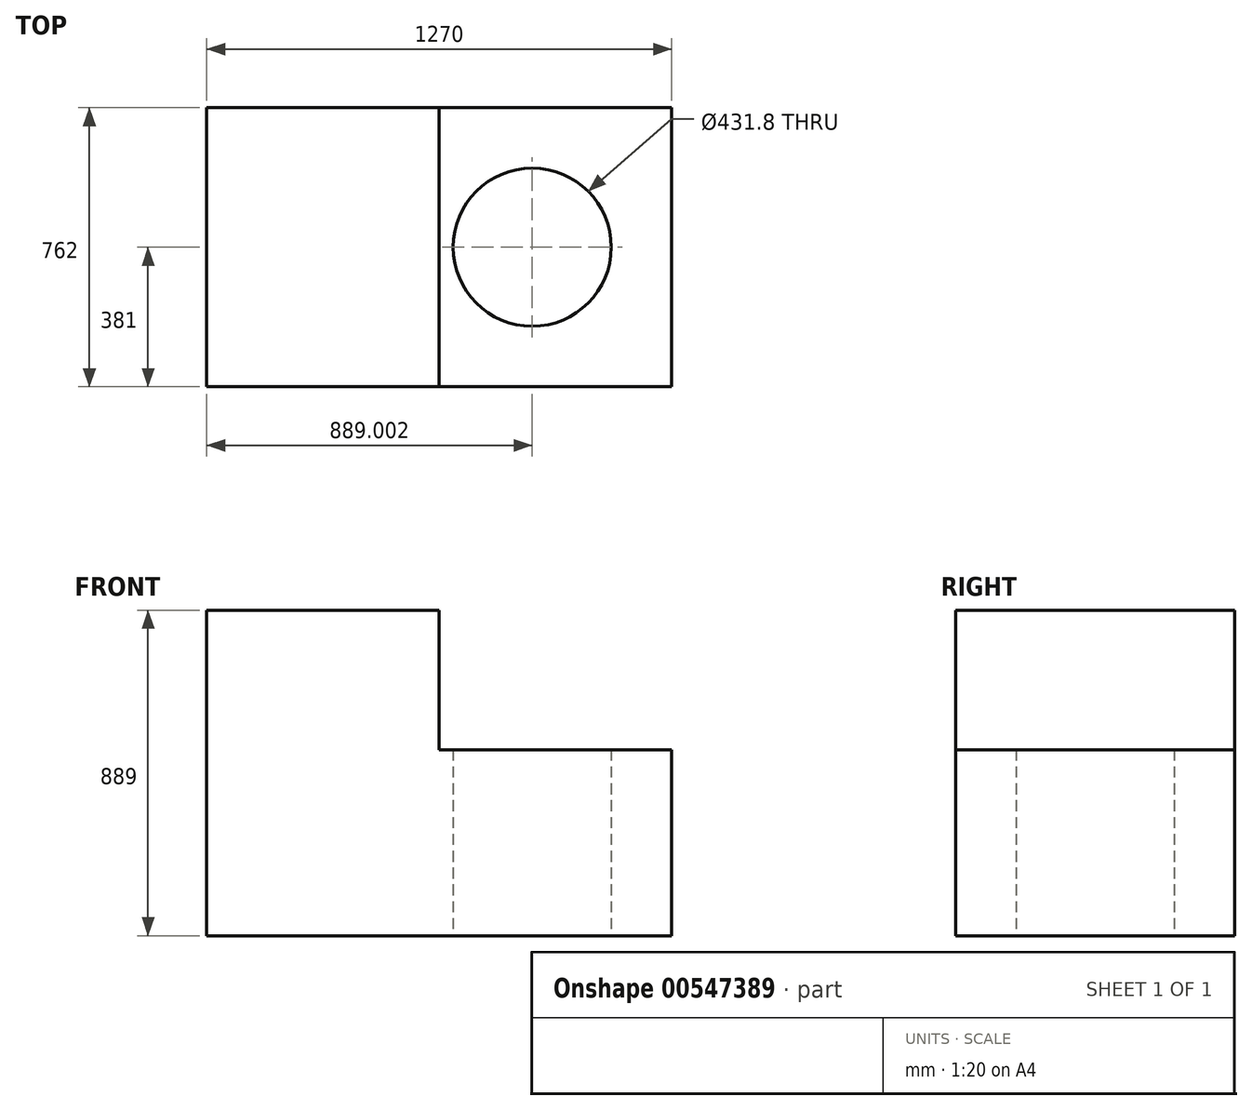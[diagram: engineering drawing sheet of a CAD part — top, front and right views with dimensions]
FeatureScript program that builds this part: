
annotation { "Feature Type Name" : "Feature", "Feature Type Description" : "" }
export const myFeature = defineFeature(function(context is Context, id is Id, definition is map)
    precondition{}
    {
        {
            var Q0;
            Q0=qCreatedBy(makeId("Front.planeOp"),FACE);
            var sketch = newSketch(context, id + "F0", { "sketchPlane" : qUnion([Q0])});
            skLineSegment(sketch, "E0", {"start": v(-633.14, -431.6) * mm, "end": v(636.86, -431.6) * mm});
            skLineSegment(sketch, "E1", {"start": v(-633.14, -431.6) * mm, "end": v(-633.14, 457.4) * mm});
            skLineSegment(sketch, "E2", {"start": v(-633.14, 457.4) * mm, "end": v(1.86, 457.4) * mm});
            skLineSegment(sketch, "E3", {"start": v(636.86, -431.6) * mm, "end": v(636.86, 76.4) * mm});
            skLineSegment(sketch, "E4", {"start": v(636.86, 76.4) * mm, "end": v(1.86, 76.4) * mm});
            skLineSegment(sketch, "E5", {"start": v(1.86, 76.4) * mm, "end": v(1.86, 457.4) * mm});
            skSolve(sketch);
        }
        {
            var Q0;
            Q0=makeQuery(id+"F0.imprint","IMPRINT",FACE,{"disambiguationData":[TD([[makeQuery(id+"F0.imprint","IMPRINT",EDGE,{"derivedFrom":sQuery(id+"F0.wireOp",EDGE,"E0")}),1.0]])]});
            var sketch = newSketch(context, id + "F1", { "sketchPlane" : qUnion([Q0])});
            skSolve(sketch);
        }
        {
            var Q0;
            Q0=qSketchRegion(id+"F0",true);
            extrude(context, id + "F2", {"entities" : qUnion([Q0]), "depth" : 381 * mm, "offsetDistance" : 25.4 * mm});
        }
        {
            var Q0;
            Q0=makeQuery(id+"F2.opExtrude","SWEPT_BODY",BODY,{"disambiguationData":[OSD([sQuery(id+"F0.wireOp",EDGE,"E0"),sQuery(id+"F0.wireOp",EDGE,"E1"),sQuery(id+"F0.wireOp",EDGE,"E2"),sQuery(id+"F0.wireOp",EDGE,"E3"),sQuery(id+"F0.wireOp",EDGE,"E4"),sQuery(id+"F0.wireOp",EDGE,"E5")])]});
            var Q1;
            Q1=makeQuery(id+"F1.imprint","IMPRINT",FACE,{"disambiguationData":[TD([[makeQuery(id+"F1.imprint","IMPRINT",EDGE,{"derivedFrom":makeQuery(id+"F0.imprint","IMPRINT",EDGE,{"derivedFrom":sQuery(id+"F0.wireOp",EDGE,"E0")})}),1.0]])]});
            mirror(context, id + "F3", {"operationType" : NewBodyOperationType.ADD, "entities" : qUnion([Q0]), "mirrorPlane" : qUnion([Q1])});
        }
        {
            var Q0;
            {var subQ0=makeQuery(id+"F2.opExtrude","SWEPT_FACE",FACE,{"disambiguationData":[OSD([sQuery(id+"F0.wireOp",EDGE,"E0")])]});Q0=makeQuery(id+"F3.boolean.opBoolean","MERGE",FACE,{"derivedFrom":[subQ0,makeQuery(id+"F3.opPattern","COPY",FACE,{"derivedFrom":subQ0,"instanceName":"1"})]});}
            var sketch = newSketch(context, id + "F4", { "sketchPlane" : qUnion([Q0])});
            skPoint(sketch, "E6.endSnap0", {"position": v(-633.14, 0) * mm});
            skCircle(sketch, "E7", {"center": v(255.86, 0) * mm, "radius": 215.9 * mm});
            skSolve(sketch);
        }
        {
            var Q0;
            Q0=makeQuery(id+"F4.imprint","IMPRINT",FACE,{"disambiguationData":[TD([[makeQuery(id+"F4.imprint","IMPRINT",EDGE,{"derivedFrom":sQuery(id+"F4.wireOp",EDGE,"E7")}),1.0]])]});
            var Q1;
            Q1=sQuery(id+"F4.wireOp",EDGE,"E7");
            extrude(context, id + "F5", {"entities" : qUnion([Q0]), "operationType" : NewBodyOperationType.REMOVE, "surfaceEntities" : qUnion([Q1]), "endBound" : BoundingType.UP_TO_NEXT, "oppositeDirection" : true, "depth" : 25.4 * mm, "offsetDistance" : 25.4 * mm});
        }
    });
